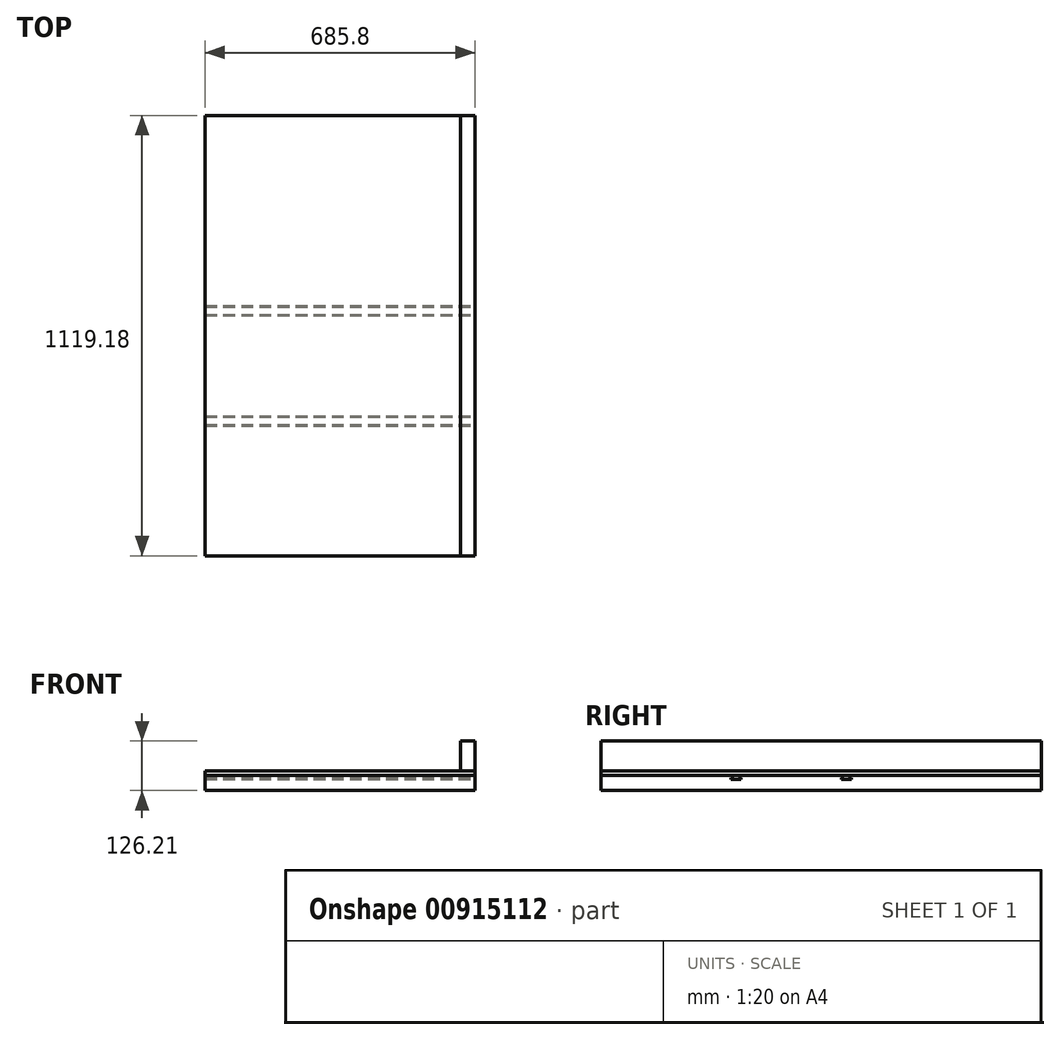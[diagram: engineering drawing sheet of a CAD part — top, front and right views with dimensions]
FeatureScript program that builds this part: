
annotation { "Feature Type Name" : "Feature", "Feature Type Description" : "" }
export const myFeature = defineFeature(function(context is Context, id is Id, definition is map)
    precondition{}
    {
        {
            var Q0;
            Q0=qCreatedBy(makeId("Top.planeOp"),FACE);
            var sketch = newSketch(context, id + "F0", { "sketchPlane" : qUnion([Q0])});
            skLineSegment(sketch, "E0.bottom", {"start": v(-342.9, 559.6) * mm, "end": v(342.9, 559.6) * mm});
            skLineSegment(sketch, "E0.top", {"start": v(-342.9, -559.6) * mm, "end": v(342.9, -559.6) * mm});
            skLineSegment(sketch, "E0.left", {"start": v(-342.9, 559.6) * mm, "end": v(-342.9, -559.6) * mm});
            skLineSegment(sketch, "E0.right", {"start": v(342.9, 559.6) * mm, "end": v(342.9, -559.6) * mm});
            skSolve(sketch);
        }
        {
            var Q0;
            Q0=makeQuery(id+"F0.imprint","IMPRINT",FACE,{"disambiguationData":[TD([[makeQuery(id+"F0.imprint","IMPRINT",EDGE,{"derivedFrom":sQuery(id+"F0.wireOp",EDGE,"E0.bottom")}),-1.0]])]});
            extrude(context, id + "F1", {"entities" : qUnion([Q0]), "depth" : 38.1 * mm});
        }
        {
            var Q0;
            Q0=makeQuery(id+"F1.opExtrude","SWEPT_FACE",FACE,{"disambiguationData":[OSD([sQuery(id+"F0.wireOp",EDGE,"E0.right")])]});
            var sketch = newSketch(context, id + "F2", { "sketchPlane" : qUnion([Q0])});
            skLineSegment(sketch, "E1", {"start": v(-226.22, 38.1) * mm, "end": v(-226.22, 32.54) * mm});
            skLineSegment(sketch, "E2", {"start": v(-226.22, 32.54) * mm, "end": v(-229.4, 32.54) * mm});
            skLineSegment(sketch, "E3", {"start": v(-229.4, 32.54) * mm, "end": v(-229.4, 28.57) * mm});
            skLineSegment(sketch, "E4", {"start": v(-229.4, 28.58) * mm, "end": v(-204, 28.58) * mm});
            skLineSegment(sketch, "E5", {"start": v(-204, 28.57) * mm, "end": v(-204, 32.54) * mm});
            skLineSegment(sketch, "E6", {"start": v(-204, 32.54) * mm, "end": v(-207.17, 32.54) * mm});
            skLineSegment(sketch, "E7", {"start": v(-207.17, 32.54) * mm, "end": v(-207.17, 38.1) * mm});
            skLineSegment(sketch, "E8", {"start": v(-226.22, 38.1) * mm, "end": v(-207.17, 38.1) * mm});
            skLineSegment(sketch, "E9", {"start": v(-216.7, 38.1) * mm, "end": v(-216.7, 28.58) * mm, "construction": true});
            skPoint(sketch, "E9.endSnap0", {"position": v(-216.7, 28.57) * mm});
            skLineSegment(sketch, "E10", {"start": v(-76.6, 38.1) * mm, "end": v(-76.6, 0) * mm, "construction": true});
            skLineSegment(sketch, "E11.MirrorCS", {"start": v(73.03, 38.1) * mm, "end": v(73.03, 32.54) * mm});
            skLineSegment(sketch, "E12.MirrorCS", {"start": v(73.03, 32.54) * mm, "end": v(76.2, 32.54) * mm});
            skLineSegment(sketch, "E13.MirrorCS", {"start": v(76.2, 32.54) * mm, "end": v(76.2, 28.58) * mm});
            skLineSegment(sketch, "E14.MirrorCS", {"start": v(76.2, 28.58) * mm, "end": v(50.8, 28.58) * mm});
            skLineSegment(sketch, "E15.MirrorCS", {"start": v(50.8, 28.58) * mm, "end": v(50.8, 32.54) * mm});
            skLineSegment(sketch, "E16.MirrorCS", {"start": v(50.8, 32.54) * mm, "end": v(53.98, 32.54) * mm});
            skLineSegment(sketch, "E17.MirrorCS", {"start": v(53.98, 32.54) * mm, "end": v(53.98, 38.1) * mm});
            skLineSegment(sketch, "E18.MirrorCS", {"start": v(73.03, 38.1) * mm, "end": v(53.98, 38.1) * mm});
            skSolve(sketch);
        }
        {
            var Q0;
            Q0=makeQuery(id+"F2.imprint","IMPRINT",FACE,{"disambiguationData":[TD([[makeQuery(id+"F2.imprint","IMPRINT",EDGE,{"derivedFrom":sQuery(id+"F2.wireOp",EDGE,"E1")}),1.0]])]});
            extrude(context, id + "F3", {"entities" : qUnion([Q0]), "operationType" : NewBodyOperationType.REMOVE, "endBound" : BoundingType.THROUGH_ALL, "oppositeDirection" : true, "depth" : 25.4 * mm});
        }
        {
            var Q0;
            Q0=makeQuery(id+"F2.imprint","IMPRINT",FACE,{"disambiguationData":[TD([[makeQuery(id+"F2.imprint","IMPRINT",EDGE,{"derivedFrom":sQuery(id+"F2.wireOp",EDGE,"E11.MirrorCS")}),-1.0]])]});
            extrude(context, id + "F4", {"entities" : qUnion([Q0]), "operationType" : NewBodyOperationType.REMOVE, "endBound" : BoundingType.THROUGH_ALL, "oppositeDirection" : true, "depth" : 25.4 * mm});
        }
        {
            var Q0;
            Q0=makeQuery(id+"F3.boolean.opBoolean","COPY",FACE,{"derivedFrom":makeQuery(id+"F3.opExtrude","SWEPT_FACE",FACE,{"disambiguationData":[OSD([sQuery(id+"F2.wireOp",EDGE,"E7")])]})});
            cPlane(context, id + "F5", {"entities" : qUnion([Q0]), "cplaneType" : CPlaneType.OFFSET, "offset" : 146.05 * mm, "oppositeDirection" : true, "width" : 152.4 * mm, "height" : 152.4 * mm});
        }
        {
            var Q0;
            Q0=makeQuery(id+"F1.opExtrude","SWEPT_FACE",FACE,{"disambiguationData":[OSD([sQuery(id+"F0.wireOp",EDGE,"E0.left")])]});
            cPlane(context, id + "F6", {"entities" : qUnion([Q0]), "cplaneType" : CPlaneType.OFFSET, "offset" : 298.45 * mm, "oppositeDirection" : true, "width" : 152.4 * mm, "height" : 152.4 * mm});
        }
        {
            var Q0;
            {var subQ0=sQuery(id+"F0.wireOp",EDGE,"E0.top");var subQ1=sQuery(id+"F0.wireOp",EDGE,"E0.left");var subQ2=sQuery(id+"F0.wireOp",EDGE,"E0.right");Q0=makeQuery(id+"F3.boolean.opBoolean","SPLIT",FACE,{"disambiguationData":[TD([makeQuery(id+"F1.opExtrude","SWEPT_FACE",FACE,{"disambiguationData":[OSD([subQ0])]})])],"derivedFrom":makeQuery(id+"F1.opExtrude","CAP_FACE",FACE,{"disambiguationData":[OSD([sQuery(id+"F0.wireOp",EDGE,"E0.bottom"),subQ0,subQ1,subQ2])],"isStart":false})});}
            var sketch = newSketch(context, id + "F7", { "sketchPlane" : qUnion([Q0])});
            skLineSegment(sketch, "E19.0", {"start": v(-342.9, 559.6) * mm, "end": v(-342.9, -559.6) * mm});
            skLineSegment(sketch, "E20.0", {"start": v(-342.9, -559.6) * mm, "end": v(342.9, -559.6) * mm});
            skLineSegment(sketch, "E21.0", {"start": v(342.9, 559.6) * mm, "end": v(342.9, -559.6) * mm});
            skLineSegment(sketch, "E22.0", {"start": v(-342.9, 559.6) * mm, "end": v(342.9, 559.6) * mm});
            skSolve(sketch);
        }
        {
            var Q0;
            Q0=qSketchRegion(id+"F7",true);
            extrude(context, id + "F8", {"entities" : qUnion([Q0]), "depth" : 11.9 * mm});
        }
        {
            var Q0;
            Q0=makeQuery(id+"F8.opExtrude","CAP_FACE",FACE,{"disambiguationData":[OSD([sQuery(id+"F7.wireOp",EDGE,"E19.0"),sQuery(id+"F7.wireOp",EDGE,"E20.0"),sQuery(id+"F7.wireOp",EDGE,"E21.0"),sQuery(id+"F7.wireOp",EDGE,"E22.0")])],"isStart":false});
            var sketch = newSketch(context, id + "F9", { "sketchPlane" : qUnion([Q0])});
            skLineSegment(sketch, "E23.0", {"start": v(342.9, 559.6) * mm, "end": v(342.9, -559.6) * mm});
            skLineSegment(sketch, "E24.0", {"start": v(306.39, -559.6) * mm, "end": v(342.9, -559.6) * mm});
            skLineSegment(sketch, "E25.0", {"start": v(306.39, 559.6) * mm, "end": v(342.9, 559.6) * mm});
            skLineSegment(sketch, "E26", {"start": v(306.39, 559.6) * mm, "end": v(306.39, -559.6) * mm});
            skPoint(sketch, "E27.orphan", {"position": v(-342.9, 559.6) * mm});
            skPoint(sketch, "E28.orphan", {"position": v(-342.9, -559.6) * mm});
            skSolve(sketch);
        }
        {
            var Q0;
            Q0=makeQuery(id+"F9.imprint","IMPRINT",FACE,{"disambiguationData":[TD([[makeQuery(id+"F9.imprint","IMPRINT",EDGE,{"derivedFrom":sQuery(id+"F9.wireOp",EDGE,"E23.0")}),-1.0]])]});
            extrude(context, id + "F10", {"entities" : qUnion([Q0]), "depth" : 76.2 * mm});
        }
        {
            var Q0;
            Q0=makeQuery(id+"F1.opExtrude","SWEPT_FACE",FACE,{"disambiguationData":[OSD([sQuery(id+"F0.wireOp",EDGE,"E0.left")])]});
            cPlane(context, id + "F11", {"entities" : qUnion([Q0]), "cplaneType" : CPlaneType.OFFSET, "offset" : 31.75 * mm, "width" : 152.4 * mm, "height" : 152.4 * mm});
        }
    });
